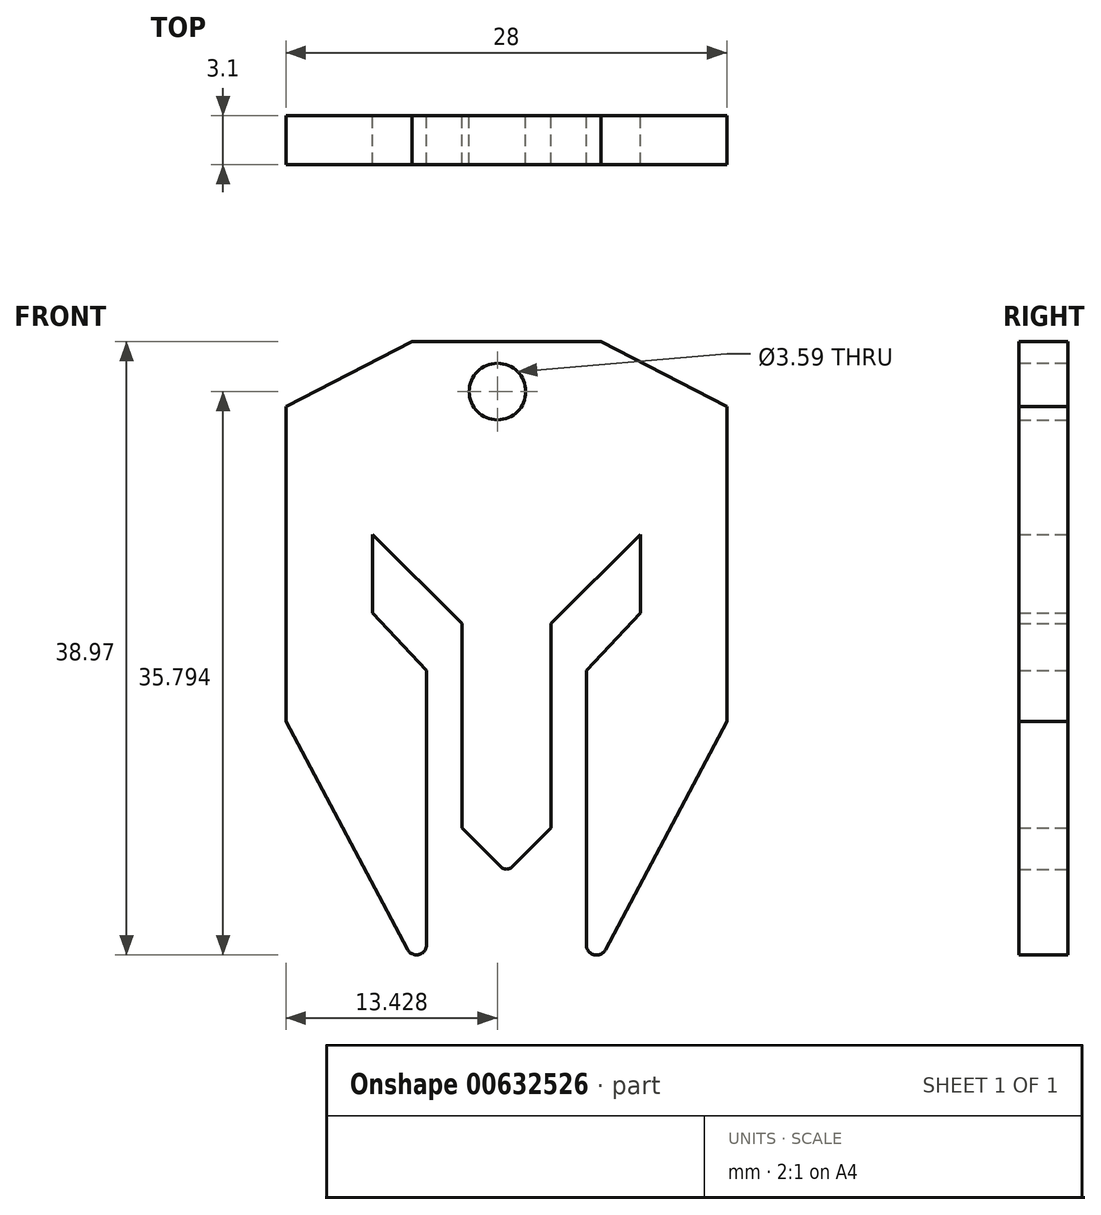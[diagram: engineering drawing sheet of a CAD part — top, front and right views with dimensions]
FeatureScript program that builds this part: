
annotation { "Feature Type Name" : "Feature", "Feature Type Description" : "" }
export const myFeature = defineFeature(function(context is Context, id is Id, definition is map)
    precondition{}
    {
        {
            var Q0;
            Q0=qCreatedBy(makeId("Front.planeOp"),FACE);
            var sketch = newSketch(context, id + "F0", { "sketchPlane" : qUnion([Q0])});
            skLineSegment(sketch, "E0", {"start": v(-33.92, 50.9) * mm, "end": v(-33.92, 30.9) * mm});
            skLineSegment(sketch, "E1", {"start": v(-33.92, 30.9) * mm, "end": v(-26.2, 16.4) * mm});
            skLineSegment(sketch, "E2", {"start": v(-25, 16.7) * mm, "end": v(-25, 34.13) * mm});
            skLineSegment(sketch, "E3", {"start": v(-25, 34.13) * mm, "end": v(-28.42, 37.77) * mm});
            skLineSegment(sketch, "E4", {"start": v(-28.42, 37.77) * mm, "end": v(-28.42, 42.77) * mm});
            skLineSegment(sketch, "E5", {"start": v(-28.42, 42.77) * mm, "end": v(-22.75, 37.13) * mm});
            skLineSegment(sketch, "E6", {"start": v(-22.75, 37.13) * mm, "end": v(-22.75, 24.13) * mm});
            skPoint(sketch, "E6.endSnap0", {"position": v(-25, 24.13) * mm});
            skLineSegment(sketch, "E7", {"start": v(-22.75, 24.13) * mm, "end": v(-20.27, 21.65) * mm});
            skLineSegment(sketch, "E8", {"start": v(-19.56, 21.65) * mm, "end": v(-17.09, 24.13) * mm});
            skLineSegment(sketch, "E9", {"start": v(-17.09, 24.13) * mm, "end": v(-17.09, 37.13) * mm});
            skLineSegment(sketch, "E10", {"start": v(-17.09, 37.13) * mm, "end": v(-11.42, 42.77) * mm});
            skLineSegment(sketch, "E11", {"start": v(-11.42, 42.77) * mm, "end": v(-11.42, 37.77) * mm});
            skLineSegment(sketch, "E12", {"start": v(-11.42, 37.77) * mm, "end": v(-14.84, 34.13) * mm});
            skLineSegment(sketch, "E13", {"start": v(-14.84, 34.13) * mm, "end": v(-14.84, 16.7) * mm});
            skLineSegment(sketch, "E14", {"start": v(-13.64, 16.39) * mm, "end": v(-5.92, 30.9) * mm});
            skLineSegment(sketch, "E15", {"start": v(-5.92, 30.9) * mm, "end": v(-5.92, 50.9) * mm});
            skLineSegment(sketch, "E16", {"start": v(-5.92, 50.9) * mm, "end": v(-13.92, 55.02) * mm});
            skLineSegment(sketch, "E17", {"start": v(-13.92, 55.02) * mm, "end": v(-25.92, 55.02) * mm});
            skLineSegment(sketch, "E18", {"start": v(-25.92, 55.02) * mm, "end": v(-33.92, 50.9) * mm});
            skCircle(sketch, "E19", {"center": v(-20.5, 51.84) * mm, "radius": 1.8 * mm});
            skPoint(sketch, "E20.visualSharp", {"position": v(-25, 14.13) * mm});
            skArc(sketch, "E20.filletArc", {"start": v(-26.2, 16.4) * mm, "mid": v(-25.48, 16.08) * mm, "end": v(-25, 16.7) * mm});
            skPoint(sketch, "E21.visualSharp", {"position": v(-14.84, 14.13) * mm});
            skArc(sketch, "E21.filletArc", {"start": v(-14.84, 16.7) * mm, "mid": v(-14.36, 16.07) * mm, "end": v(-13.64, 16.39) * mm});
            skPoint(sketch, "E22.visualSharp", {"position": v(-19.92, 21.3) * mm});
            skArc(sketch, "E22.filletArc", {"start": v(-20.27, 21.65) * mm, "mid": v(-19.92, 21.5) * mm, "end": v(-19.56, 21.65) * mm});
            skSolve(sketch);
        }
        {
            var Q0;
            Q0=makeQuery(id+"F0.imprint","IMPRINT",FACE,{"disambiguationData":[TD([[makeQuery(id+"F0.imprint","IMPRINT",EDGE,{"derivedFrom":sQuery(id+"F0.wireOp",EDGE,"E0")}),1.0]])]});
            extrude(context, id + "F1", {"entities" : qUnion([Q0]), "depth" : 3.1 * mm, "offsetDistance" : 25 * mm});
        }
    });
